# Revit family: MT-HB_BIFOLD DOOR_XXXXXXX
name_source: partatom
category: Doors
revit_build: Autodesk Revit 2017 (Build: 20160225_1515(x64)
units: mm (PartAtom-declared; Revit-internal decimal feet)

## family parameters
Always vertical = Yes
Cut with Voids When Loaded = No
Host = Wall
OmniClass Number = 23.30.20.00
OmniClass Title = Windows
Room Calculation Point = No
Shared = No

## types (3) — shared parameters
101.6mm FRAME THICKNESS = No
150mm FRAME THICKNESS = Yes
7L/7R = No
A = 4 mm  [stored 0.0131234 ft]
ANZRC COMPLIANT = YES
Analytic Construction = <None>
BOT PANEL POSITION = 95 mm
DETAIL_DEPTH SILL = 150 mm
DOUBLE GLAZED = No
DOUBLE GLAZED THICKNESS = 18 mm  [stored 0.0590551 ft]
FRAME MATERIAL = <By Category>
FRAME THICKNESS = 76 mm  [stored 0.249344 ft]
GLAZED MATERIAL = Glass
MAX HEIGHT = 3000 mm  [stored 9.84252 ft]
MAX PANEL HEIGHT = 3000 mm  [stored 9.84252 ft]
MAX PANEL WIDTH = 1000 mm  [stored 3.28084 ft]
MAX WIDTH = 7000 mm
Manufacturer = ALSPEC
Model = HAWKESBURY TOP HUNG COMMERCIAL MULTI-FOLD DOOR
OFFSET = 10 mm  [stored 0.0328084 ft]
SINGLE GLAZED THICKNESS = 5 mm  [stored 0.0164042 ft]
URL = WWW.ALSPEC.COM.AU
VERSION = 2.1
WARNING = No
Wall Closure = By host
YEAR = 2019
zero-valued in all types: Default Sill Height, TOLERANCE

## per-type parameters (varying)
| type | 4L3R/3L4R | 5L2R/2L5R | AIR POCKET | Height | OVERALL FRAME HEIGHT | OVERALL FRAME WIDTH | PANEL HEIGHT | PANEL WIDTH | Rough Height | Rough Width | TOP PANEL POSITION | Width |
| 7L/7R | No | Yes | 8 mm  [stored 0.0262467 ft] | 2100 mm | 2100 mm | 5500 mm  [stored 18.0446 ft] | 1907 mm | 768 mm | 2100 mm | 5500 mm  [stored 18.0446 ft] | 1891 mm | 5500 mm  [stored 18.0446 ft] |
| 4L3R/3L4R | Yes | No | 5 mm  [stored 0.0164042 ft] | 2700 mm | 2700 mm | 6500 mm  [stored 21.3255 ft] | 2507 mm | 911 mm | 2700 mm | 6500 mm  [stored 21.3255 ft] | 2491 mm | 6500 mm  [stored 21.3255 ft] |
| 5L2R/2L5R | No | Yes | 8 mm  [stored 0.0262467 ft] | 2100 mm | 2100 mm | 5500 mm  [stored 18.0446 ft] | 1907 mm | 768 mm | 2100 mm | 5500 mm  [stored 18.0446 ft] | 1891 mm | 5500 mm  [stored 18.0446 ft] |

note: [stored X ft] marks values corroborated as IEEE doubles in the binary element streams (Revit-internal decimal feet)

## geometry (parser evidence)
native form markers: Extrusion x1, Sweep x30
no freeform markers — native parametric forms only
